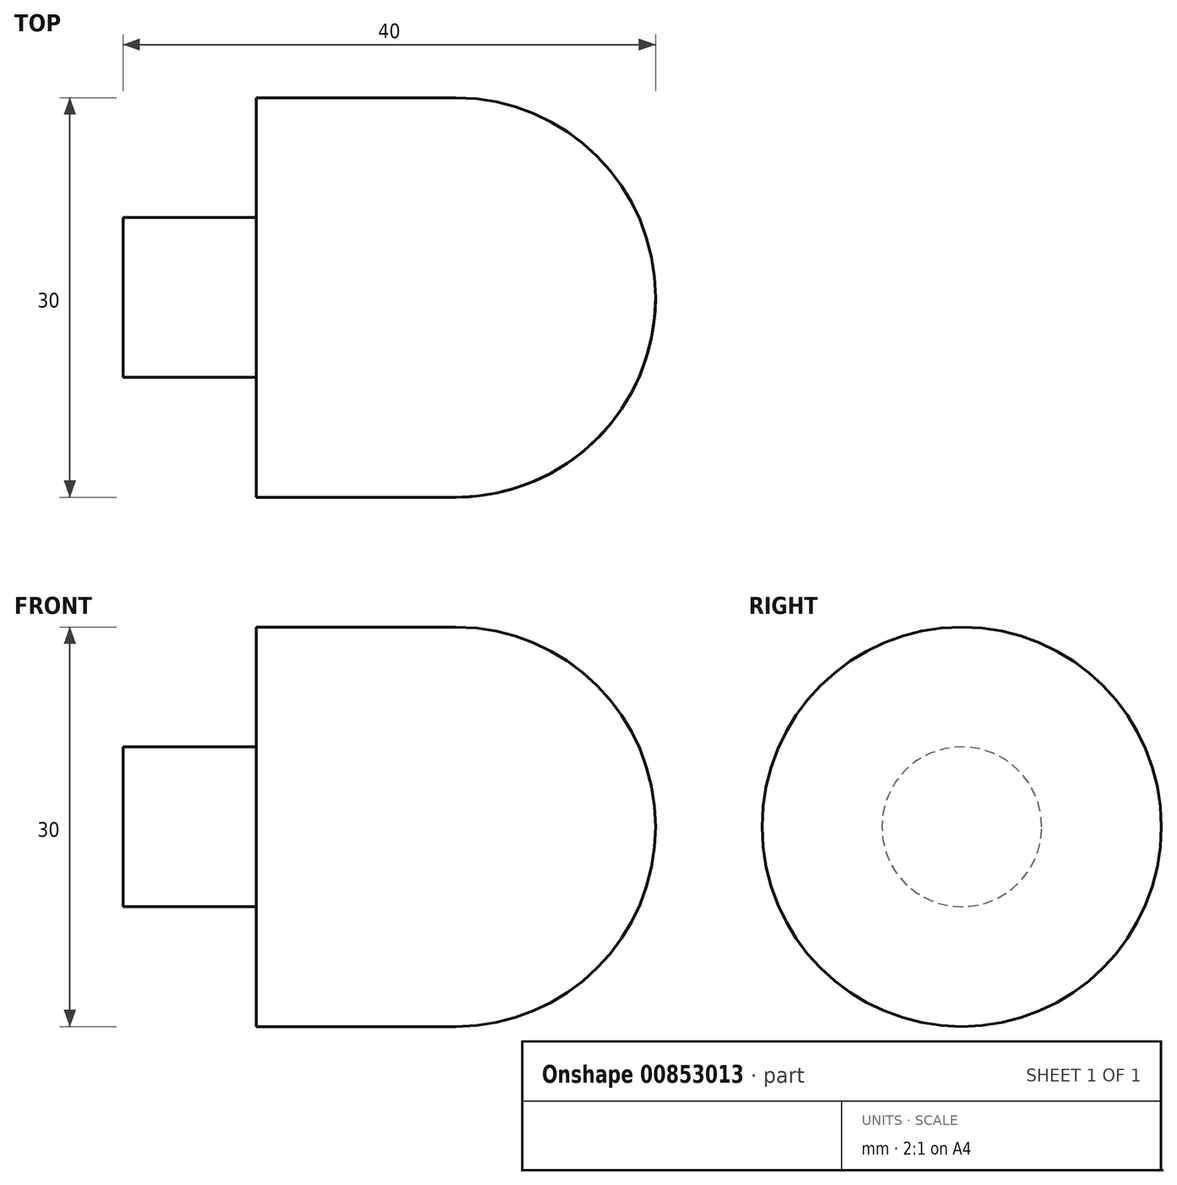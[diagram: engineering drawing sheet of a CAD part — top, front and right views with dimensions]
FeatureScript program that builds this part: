
annotation { "Feature Type Name" : "Feature", "Feature Type Description" : "" }
export const myFeature = defineFeature(function(context is Context, id is Id, definition is map)
    precondition{}
    {
        {
            var Q0;
            Q0=qCreatedBy(makeId("Top.planeOp"),FACE);
            var sketch = newSketch(context, id + "F0", { "sketchPlane" : qUnion([Q0])});
            skLineSegment(sketch, "E0", {"start": v(0, 0) * mm, "end": v(0, 6) * mm});
            skLineSegment(sketch, "E1", {"start": v(0, 6) * mm, "end": v(10, 6) * mm});
            skLineSegment(sketch, "E2", {"start": v(10, 6) * mm, "end": v(10, 15) * mm});
            skLineSegment(sketch, "E3", {"start": v(10, 15) * mm, "end": v(25, 15) * mm});
            skLineSegment(sketch, "E4", {"start": v(25, 15) * mm, "end": v(25, 15) * mm});
            skLineSegment(sketch, "E5", {"start": v(40, 0) * mm, "end": v(40, 0) * mm});
            skLineSegment(sketch, "E6", {"start": v(40, 0) * mm, "end": v(0, 0) * mm});
            skPoint(sketch, "E7.visualSharp", {"position": v(40, 15) * mm});
            skArc(sketch, "E7.filletArc", {"start": v(40, 0) * mm, "mid": v(35.6, 10.6) * mm, "end": v(25, 15) * mm});
            skSolve(sketch);
        }
        {
            var Q0;
            Q0=qSketchRegion(id+"F0",true);
            var Q1;
            Q1=sQuery(id+"F0.wireOp",EDGE,"E6");
            revolve(context, id + "F1", {"surfaceOperationType" : NewSurfaceOperationType.NEW, "entities" : qUnion([Q0]), "axis" : qUnion([Q1]), "revolveType" : RevolveType.FULL});
        }
    });
